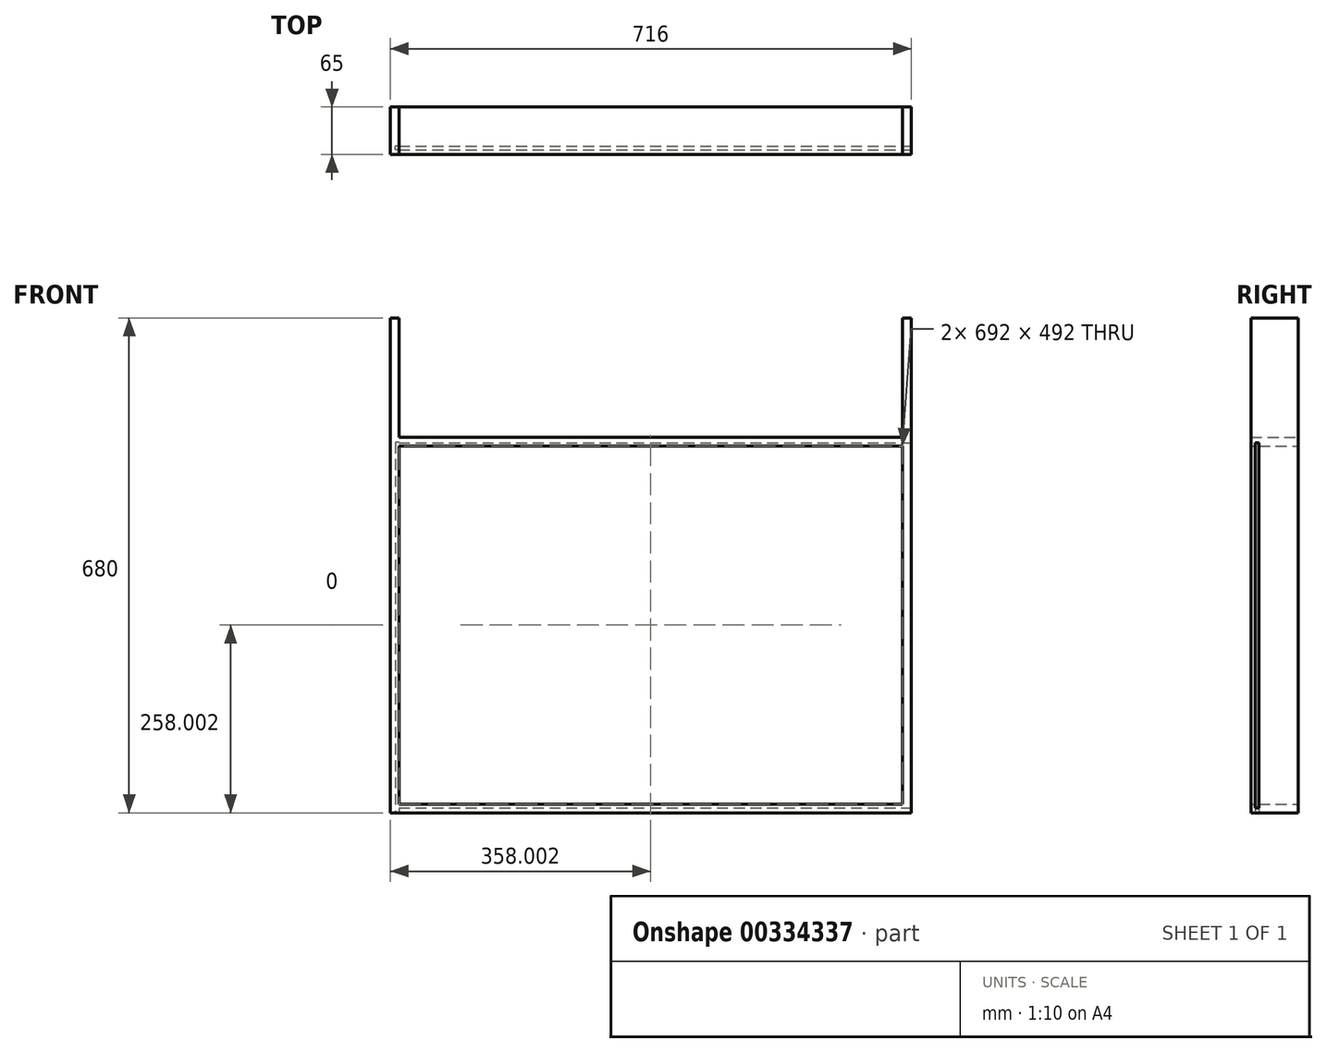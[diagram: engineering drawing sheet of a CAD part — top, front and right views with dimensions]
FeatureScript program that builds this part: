
annotation { "Feature Type Name" : "Feature", "Feature Type Description" : "" }
export const myFeature = defineFeature(function(context is Context, id is Id, definition is map)
    precondition{}
    {
        {
            var Q0;
            Q0=qCreatedBy(makeId("Front.planeOp"),FACE);
            var sketch = newSketch(context, id + "F0", { "sketchPlane" : qUnion([Q0])});
            skLineSegment(sketch, "E0.bottom", {"start": v(-644.48, 630.9) * mm, "end": v(-632.48, 630.9) * mm});
            skLineSegment(sketch, "E0.top", {"start": v(-644.48, -49.1) * mm, "end": v(-632.48, -49.1) * mm});
            skLineSegment(sketch, "E0.left", {"start": v(-644.48, 630.9) * mm, "end": v(-644.48, -49.1) * mm});
            skLineSegment(sketch, "E0.right", {"start": v(-632.48, 630.9) * mm, "end": v(-632.48, 466.9) * mm});
            skLineSegment(sketch, "E1.bottom", {"start": v(59.52, 630.9) * mm, "end": v(71.52, 630.9) * mm});
            skLineSegment(sketch, "E1.top", {"start": v(59.52, -49.1) * mm, "end": v(71.52, -49.1) * mm});
            skLineSegment(sketch, "E1.left", {"start": v(59.52, 630.9) * mm, "end": v(59.52, 466.9) * mm});
            skLineSegment(sketch, "E1.right", {"start": v(71.52, 630.9) * mm, "end": v(71.52, -49.1) * mm});
            skLineSegment(sketch, "E2.bottom", {"start": v(59.52, -49.1) * mm, "end": v(-632.48, -49.1) * mm});
            skLineSegment(sketch, "E2.top", {"start": v(59.52, -37.1) * mm, "end": v(-632.48, -37.1) * mm});
            skLineSegment(sketch, "E2.left", {"start": v(59.52, -49.1) * mm, "end": v(59.52, -37.1) * mm});
            skLineSegment(sketch, "E2.right", {"start": v(-632.48, -49.1) * mm, "end": v(-632.48, -37.1) * mm});
            skLineSegment(sketch, "E3.bottom", {"start": v(59.52, 630.9) * mm, "end": v(-634.48, 630.9) * mm});
            skLineSegment(sketch, "E3.top", {"start": v(59.52, 618.9) * mm, "end": v(-632.48, 618.9) * mm});
            skLineSegment(sketch, "E3.left", {"start": v(59.52, 630.9) * mm, "end": v(59.52, 618.9) * mm});
            skLineSegment(sketch, "E3.right", {"start": v(-632.48, 630.9) * mm, "end": v(-632.48, 618.9) * mm});
            skLineSegment(sketch, "E4.left", {"start": v(63.52, 454.9) * mm, "end": v(63.52, 466.9) * mm});
            skLineSegment(sketch, "E4.right", {"start": v(-636.48, 454.9) * mm, "end": v(-636.48, 466.9) * mm});
            skLineSegment(sketch, "E5.trimOffspring", {"start": v(59.52, 454.9) * mm, "end": v(59.52, -49.1) * mm});
            skLineSegment(sketch, "E6.trimOffspring", {"start": v(-632.48, 454.9) * mm, "end": v(-632.48, -49.1) * mm});
            skLineSegment(sketch, "E7", {"start": v(-636.48, 466.9) * mm, "end": v(63.52, 466.9) * mm});
            skLineSegment(sketch, "E8", {"start": v(-636.48, 454.9) * mm, "end": v(63.52, 454.9) * mm});
            skSolve(sketch);
        }
        {
            var Q0;
            {var subQ4=sQuery(id+"F0.wireOp",EDGE,"E4.left");Q0=makeQuery(id+"F0.imprint","IMPRINT",FACE,{"disambiguationData":[TD([[makeQuery(id+"F0.imprint","IMPRINT",EDGE,{"derivedFrom":subQ4}),1.0]])]});}
            var Q1;
            Q1=makeQuery(id+"F0.imprint","IMPRINT",FACE,{"disambiguationData":[TD([[makeQuery(id+"F0.imprint","IMPRINT",EDGE,{"derivedFrom":sQuery(id+"F0.wireOp",EDGE,"E0.bottom")}),-1.0]])]});
            var Q2;
            {var subQ5=sQuery(id+"F0.wireOp",EDGE,"E3.left");Q2=makeQuery(id+"F0.imprint","IMPRINT",FACE,{"disambiguationData":[TD([[makeQuery(id+"F0.imprint","IMPRINT",EDGE,{"derivedFrom":subQ5}),-1.0]])]});}
            var Q3;
            Q3=makeQuery(id+"F0.imprint","IMPRINT",FACE,{"disambiguationData":[TD([[makeQuery(id+"F0.imprint","IMPRINT",EDGE,{"derivedFrom":sQuery(id+"F0.wireOp",EDGE,"E1.bottom")}),-1.0]])]});
            var Q4;
            {var subQ0=sQuery(id+"F0.wireOp",EDGE,"E2.bottom");Q4=makeQuery(id+"F0.imprint","IMPRINT",FACE,{"disambiguationData":[TD([[makeQuery(id+"F0.imprint","IMPRINT",EDGE,{"derivedFrom":subQ0}),-1.0]])]});}
            extrude(context, id + "F1", {"entities" : qUnion([Q0, Q1, Q2, Q3, Q4]), "depth" : 65 * mm});
        }
        {
            var Q0;
            Q0=makeQuery(id+"F1.opExtrude","SWEPT_FACE",FACE,{"disambiguationData":[OSD([sQuery(id+"F0.wireOp",EDGE,"E1.right")])]});
            var sketch = newSketch(context, id + "F2", { "sketchPlane" : qUnion([Q0])});
            skLineSegment(sketch, "E9.bottom", {"start": v(-59, -37.1) * mm, "end": v(-54, -37.1) * mm});
            skLineSegment(sketch, "E9.top", {"start": v(-59, -42.1) * mm, "end": v(-54, -42.1) * mm});
            skLineSegment(sketch, "E9.left", {"start": v(-59, -37.1) * mm, "end": v(-59, -42.1) * mm});
            skLineSegment(sketch, "E9.right", {"start": v(-54, -37.1) * mm, "end": v(-54, -42.1) * mm});
            skSolve(sketch);
        }
        {
            var Q0;
            Q0=makeQuery(id+"F2.imprint","IMPRINT",FACE,{"disambiguationData":[TD([[makeQuery(id+"F2.imprint","IMPRINT",EDGE,{"derivedFrom":sQuery(id+"F2.wireOp",EDGE,"E9.bottom")}),-1.0]])]});
            extrude(context, id + "F3", {"entities" : qUnion([Q0]), "operationType" : NewBodyOperationType.REMOVE, "oppositeDirection" : true, "depth" : 709 * mm});
        }
        {
            var Q0;
            Q0=makeQuery(id+"F1.opExtrude","SWEPT_FACE",FACE,{"disambiguationData":[OSD([sQuery(id+"F0.wireOp",EDGE,"E1.right")])]});
            var sketch = newSketch(context, id + "F4", { "sketchPlane" : qUnion([Q0])});
            skLineSegment(sketch, "E10.bottom", {"start": v(-59, 459.33) * mm, "end": v(-54, 459.33) * mm});
            skLineSegment(sketch, "E10.top", {"start": v(-59, 454.9) * mm, "end": v(-54, 454.9) * mm});
            skLineSegment(sketch, "E10.left", {"start": v(-59, 459.33) * mm, "end": v(-59, 454.9) * mm});
            skLineSegment(sketch, "E10.right", {"start": v(-54, 459.33) * mm, "end": v(-54, 454.9) * mm});
            skSolve(sketch);
        }
        {
            var Q0;
            Q0 = qSketchRegion(id + "F4", true);
            extrude(context, id + "F5", {"entities" : qUnion([Q0]), "operationType" : NewBodyOperationType.REMOVE, "oppositeDirection" : true, "depth" : 709 * mm});
        }
        {
            var Q0;
            Q0=makeQuery(id+"F1.opExtrude","SWEPT_FACE",FACE,{"disambiguationData":[OSD([sQuery(id+"F0.wireOp",EDGE,"E0.top"),sQuery(id+"F0.wireOp",EDGE,"E1.top"),sQuery(id+"F0.wireOp",EDGE,"E2.bottom")])]});
            var sketch = newSketch(context, id + "F6", { "sketchPlane" : qUnion([Q0])});
            skLineSegment(sketch, "E11.bottom", {"start": v(-632.48, 59) * mm, "end": v(-637.48, 59) * mm});
            skLineSegment(sketch, "E11.top", {"start": v(-632.48, 54) * mm, "end": v(-637.48, 54) * mm});
            skLineSegment(sketch, "E11.left", {"start": v(-632.48, 59) * mm, "end": v(-632.48, 54) * mm});
            skLineSegment(sketch, "E11.right", {"start": v(-637.48, 59) * mm, "end": v(-637.48, 54) * mm});
            skSolve(sketch);
        }
        {
            var Q0;
            Q0=makeQuery(id+"F6.imprint","IMPRINT",FACE,{"disambiguationData":[TD([[makeQuery(id+"F6.imprint","IMPRINT",EDGE,{"derivedFrom":sQuery(id+"F6.wireOp",EDGE,"E11.bottom")}),1.0]])]});
            extrude(context, id + "F7", {"entities" : qUnion([Q0]), "operationType" : NewBodyOperationType.REMOVE, "oppositeDirection" : true, "depth" : 509 * mm});
        }
        {
            var Q0;
            Q0=makeQuery(id+"F1.opExtrude","SWEPT_FACE",FACE,{"disambiguationData":[OSD([sQuery(id+"F0.wireOp",EDGE,"E1.right")])]});
            var sketch = newSketch(context, id + "F8", { "sketchPlane" : qUnion([Q0])});
            skLineSegment(sketch, "E12.bottom", {"start": v(-59, 454.9) * mm, "end": v(-54, 454.9) * mm});
            skLineSegment(sketch, "E12.top", {"start": v(-59, -37.1) * mm, "end": v(-54, -37.1) * mm});
            skLineSegment(sketch, "E12.left", {"start": v(-59, 454.9) * mm, "end": v(-59, -37.1) * mm});
            skLineSegment(sketch, "E12.right", {"start": v(-54, 454.9) * mm, "end": v(-54, -37.1) * mm});
            skSolve(sketch);
        }
        {
            var Q0;
            Q0=makeQuery(id+"F8.imprint","IMPRINT",FACE,{"disambiguationData":[TD([[makeQuery(id+"F8.imprint","IMPRINT",EDGE,{"derivedFrom":sQuery(id+"F8.wireOp",EDGE,"E12.bottom")}),-1.0]])]});
            extrude(context, id + "F9", {"entities" : qUnion([Q0]), "operationType" : NewBodyOperationType.REMOVE, "oppositeDirection" : true, "depth" : 12 * mm});
        }
    });
